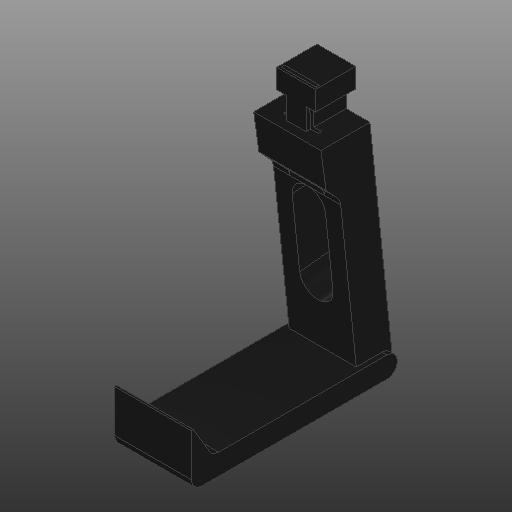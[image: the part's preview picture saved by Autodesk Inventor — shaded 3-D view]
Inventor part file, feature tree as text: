
AUTODESK INVENTOR PART (.ipt)
format: ipt  version: 2020 (Build 240168000, 168)  size: 344,064 bytes
history: native  units: in
note: dims shown in document units (in); Inventor stores cm internally (conversion verified against a paired STEP export)
features: extrude x5, other x3
ambient origin geometry x8: Origin, YZ Plane, XZ Plane, XY Plane, X Axis, Y Axis, Z Axis, Center Point
bodies: Solid1 (feature_tree)
feature tree (8):
  other  "Neck Start Plane"
  other  "Arm Profile"
  extrude  "Main Arm"  Depth=0.0049in
  extrude  "Pincher"  Depth=1.0534in
  extrude  "Neck"  Depth=0.7283in
  extrude  "Spring Steel Slot"  Depth=0.1181in
  extrude  "Viewport"  TaperAngle=0.0deg  [1 undecoded]
  other  "Neck Sketch"
note: 1 required parameter value undecoded (feature->parameter linkage not recoverable at this tier; creation-order binding heuristic only, values carry confidence <= 0.55)
